# Revit family: Legrand_Coffrets HYPRA équipés 3 prises IP55-66 avec disjoncteur + interdifférentiel
name_source: partatom
category: Equipement électrique
units: mm (PartAtom-declared; Revit-internal decimal feet)

## family parameters
Basée sur le plan de construction = Non
Configuration du panneau = Deux colonnes, circuits au sein
Cote de connecteur circulaire = Utiliser le diamètre
Couper avec des vides une fois chargée = Non
Numéro OmniClass = 23.80.30.11.17
Partagée = Non
Point de calcul de pièce = Non
Titre OmniClass = Distribution Boards and Control Panels
Toujours verticalement = Oui
Type d'élément = Tableau de raccordement

## types (2) — shared parameters
Classe de protection = IP55/66
Conditions Générale d'Utilisation = https://export.legrand.com
Description = Coffret multiprise Hypra équipé
Fabricant = Legrand
IEC 61439-2 = 40A
IEC 61439-3 = 40A
Nombre de prise 2P+T 16A = 1 tension 200 à 250 V
Nombre de prise 2P+T NFC 16A = 1 tension 200 à 250 V
Protection = Disjoncteur + interdifférentiel
URL = www.legrand.fr
zero-valued in all types: Elévation par défaut

## per-type parameters (varying)
| type | Nombre de prise 3P+T 16A | Nombre de prise 3P+T 32A |
| Référence 059874 |  | 1 tension 380 à 415 V |
| Référence 059875 | 1 tension 380 à 415 V |  |

note: column(s) folded — value = type name in every type: Modèle
